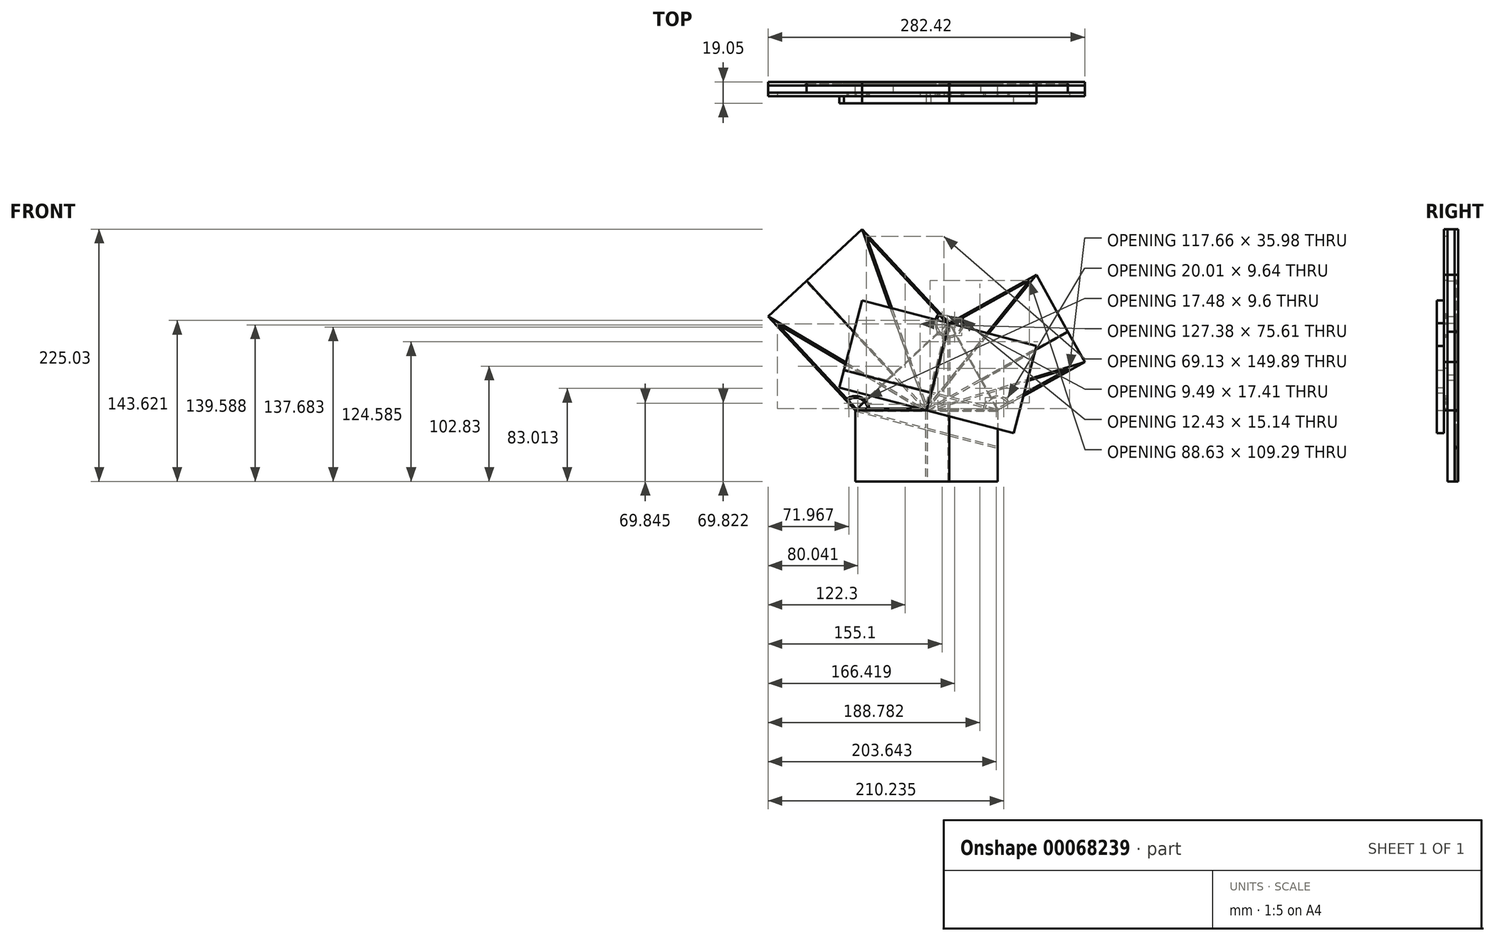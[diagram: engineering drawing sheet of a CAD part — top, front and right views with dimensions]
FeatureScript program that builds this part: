
annotation { "Feature Type Name" : "Feature", "Feature Type Description" : "" }
export const myFeature = defineFeature(function(context is Context, id is Id, definition is map)
    precondition{}
    {
        {
            var Q0;
            Q0=qCreatedBy(makeId("Front.planeOp"),FACE);
            var sketch = newSketch(context, id + "F0", { "sketchPlane" : qUnion([Q0])});
            skLineSegment(sketch, "E0", {"start": v(0, 0) * mm, "end": v(20.32, 77.7) * mm});
            skLineSegment(sketch, "E1", {"start": v(-63.5, 0) * mm, "end": v(63.5, 0) * mm, "construction": true});
            skLineSegment(sketch, "E2", {"start": v(63.5, 0) * mm, "end": v(20.32, 77.7) * mm});
            skLineSegment(sketch, "E3", {"start": v(20.32, 77.7) * mm, "end": v(-63.5, 0) * mm});
            skLineSegment(sketch, "E4.top", {"start": v(-63.5, -63.5) * mm, "end": v(63.5, -63.5) * mm});
            skLineSegment(sketch, "E4.left", {"start": v(-63.5, 0) * mm, "end": v(-63.5, -63.5) * mm});
            skLineSegment(sketch, "E4.right", {"start": v(63.5, 0) * mm, "end": v(63.5, -63.5) * mm});
            skLineSegment(sketch, "E5", {"start": v(-63.5, 0) * mm, "end": v(-141.2, 83.82) * mm});
            skLineSegment(sketch, "E6", {"start": v(-141.2, 83.82) * mm, "end": v(-57.39, 161.53) * mm});
            skLineSegment(sketch, "E7", {"start": v(-57.39, 161.53) * mm, "end": v(20.32, 77.7) * mm});
            skLineSegment(sketch, "E8", {"start": v(20.32, 77.7) * mm, "end": v(98.03, 120.89) * mm});
            skLineSegment(sketch, "E9", {"start": v(98.03, 120.89) * mm, "end": v(141.2, 43.18) * mm});
            skLineSegment(sketch, "E10", {"start": v(141.2, 43.18) * mm, "end": v(63.5, 0) * mm});
            skLineSegment(sketch, "E11", {"start": v(20.32, 77.7) * mm, "end": v(20.32, -63.5) * mm, "construction": true});
            skLineSegment(sketch, "E12", {"start": v(0, 0) * mm, "end": v(126.23, 70.14) * mm, "construction": true});
            skLineSegment(sketch, "E13", {"start": v(0, 0) * mm, "end": v(-107.06, 115.48) * mm, "construction": true});
            skLineSegment(sketch, "E14", {"start": v(0, 0) * mm, "end": v(-63.5, 0) * mm});
            skLineSegment(sketch, "E15", {"start": v(0, 0) * mm, "end": v(63.5, 0) * mm});
            skLineSegment(sketch, "E16", {"start": v(20.32, 77.7) * mm, "end": v(98.03, 57.39) * mm, "construction": true});
            skLineSegment(sketch, "E17", {"start": v(98.03, 57.39) * mm, "end": v(77.7, -20.32) * mm, "construction": true});
            skLineSegment(sketch, "E18", {"start": v(77.7, -20.32) * mm, "end": v(0, 0) * mm, "construction": true});
            skLineSegment(sketch, "E19", {"start": v(20.32, 77.7) * mm, "end": v(-57.39, 98.03) * mm, "construction": true});
            skLineSegment(sketch, "E20", {"start": v(-57.39, 98.03) * mm, "end": v(-77.7, 20.32) * mm, "construction": true});
            skLineSegment(sketch, "E21", {"start": v(-77.7, 20.32) * mm, "end": v(0, 0) * mm, "construction": true});
            skLineSegment(sketch, "E22", {"start": v(63.5, 0) * mm, "end": v(4.06, 15.54) * mm, "construction": true});
            skLineSegment(sketch, "E23", {"start": v(4.06, 15.54) * mm, "end": v(-73.65, 35.86) * mm, "construction": true});
            skLineSegment(sketch, "E24", {"start": v(0, 0) * mm, "end": v(0, -63.5) * mm, "construction": true});
            skLineSegment(sketch, "E25", {"start": v(77.7, -20.32) * mm, "end": v(73.65, -35.86) * mm, "construction": true});
            skLineSegment(sketch, "E26", {"start": v(73.65, -35.86) * mm, "end": v(-63.5, 0) * mm, "construction": true});
            skLineSegment(sketch, "E27", {"start": v(0, 0) * mm, "end": v(-4.06, -15.54) * mm, "construction": true});
            skLineSegment(sketch, "E28", {"start": v(20.32, 0) * mm, "end": v(20.32, -63.5) * mm});
            skLineSegment(sketch, "E29", {"start": v(126.23, 70.14) * mm, "end": v(48.52, 26.96) * mm});
            skLineSegment(sketch, "E30", {"start": v(-107.06, 115.48) * mm, "end": v(-29.35, 31.66) * mm});
            skSolve(sketch);
        }
        {
            var Q0;
            {var subQ0=sQuery(id+"F0.wireOp",EDGE,"E0");Q0=makeQuery(id+"F0.imprint","IMPRINT",FACE,{"disambiguationData":[TD([[makeQuery(id+"F0.imprint","IMPRINT",EDGE,{"derivedFrom":subQ0}),1.0]])]});}
            var Q1;
            {var subQ1=sQuery(id+"F0.wireOp",EDGE,"E0");Q1=makeQuery(id+"F0.imprint","IMPRINT",FACE,{"disambiguationData":[TD([[makeQuery(id+"F0.imprint","IMPRINT",EDGE,{"derivedFrom":subQ1}),-1.0]])]});}
            var Q2;
            {var subQ0=sQuery(id+"F0.wireOp",EDGE,"E7");Q2=makeQuery(id+"F0.imprint","IMPRINT",FACE,{"disambiguationData":[TD([[makeQuery(id+"F0.imprint","IMPRINT",EDGE,{"derivedFrom":subQ0}),-1.0]])]});}
            var Q3;
            {var subQ0=sQuery(id+"F0.wireOp",EDGE,"E5");Q3=makeQuery(id+"F0.imprint","IMPRINT",FACE,{"disambiguationData":[TD([[makeQuery(id+"F0.imprint","IMPRINT",EDGE,{"derivedFrom":subQ0}),-1.0]])]});}
            var Q4;
            {var subQ0=sQuery(id+"F0.wireOp",EDGE,"E8");Q4=makeQuery(id+"F0.imprint","IMPRINT",FACE,{"disambiguationData":[TD([[makeQuery(id+"F0.imprint","IMPRINT",EDGE,{"derivedFrom":subQ0}),-1.0]])]});}
            var Q5;
            {var subQ0=sQuery(id+"F0.wireOp",EDGE,"E10");Q5=makeQuery(id+"F0.imprint","IMPRINT",FACE,{"disambiguationData":[TD([[makeQuery(id+"F0.imprint","IMPRINT",EDGE,{"derivedFrom":subQ0}),-1.0]])]});}
            var Q6;
            {var subQ0=sQuery(id+"F0.wireOp",EDGE,"E4.right");Q6=makeQuery(id+"F0.imprint","IMPRINT",FACE,{"disambiguationData":[TD([[makeQuery(id+"F0.imprint","IMPRINT",EDGE,{"derivedFrom":subQ0}),-1.0]])]});}
            var Q7;
            {var subQ3=sQuery(id+"F0.wireOp",EDGE,"E4.left");Q7=makeQuery(id+"F0.imprint","IMPRINT",FACE,{"disambiguationData":[TD([[makeQuery(id+"F0.imprint","IMPRINT",EDGE,{"derivedFrom":subQ3}),1.0]])]});}
            extrude(context, id + "F1", {"entities" : qUnion([Q0, Q1, Q2, Q3, Q4, Q5, Q6, Q7]), "oppositeDirection" : true, "depth" : 3.17 * mm});
        }
        {
            var Q0;
            Q0=makeQuery(id+"F1.opExtrude","CAP_FACE",FACE,{"disambiguationData":[OSD([sQuery(id+"F0.wireOp",EDGE,"E4.top"),sQuery(id+"F0.wireOp",EDGE,"E4.left"),sQuery(id+"F0.wireOp",EDGE,"E4.right"),sQuery(id+"F0.wireOp",EDGE,"E5"),sQuery(id+"F0.wireOp",EDGE,"E6"),sQuery(id+"F0.wireOp",EDGE,"E7"),sQuery(id+"F0.wireOp",EDGE,"E8"),sQuery(id+"F0.wireOp",EDGE,"E9"),sQuery(id+"F0.wireOp",EDGE,"E10")])],"isStart":true});
            var sketch = newSketch(context, id + "F2", { "sketchPlane" : qUnion([Q0])});
            skLineSegment(sketch, "E31", {"start": v(20.32, 77.7) * mm, "end": v(-63.5, 0) * mm});
            skLineSegment(sketch, "E32", {"start": v(-63.5, 0) * mm, "end": v(63.5, 0) * mm});
            skLineSegment(sketch, "E33", {"start": v(63.5, 0) * mm, "end": v(20.32, 77.7) * mm});
            skArc(sketch, "E34.0.startCap", {"start": v(-63.5, -0.76) * mm, "mid": v(-64.26, 0) * mm, "end": v(-63.5, 0.76) * mm});
            skArc(sketch, "E34.0.endCap", {"start": v(63.5, 0.76) * mm, "mid": v(64.26, 0) * mm, "end": v(63.5, -0.76) * mm});
            skLineSegment(sketch, "E34.0.left", {"start": v(-63.5, 0.76) * mm, "end": v(62.2, 0.76) * mm});
            skLineSegment(sketch, "E34.0.right", {"start": v(-63.5, -0.76) * mm, "end": v(63.5, -0.76) * mm});
            skArc(sketch, "E34.1.startCap", {"start": v(19.8, 78.27) * mm, "mid": v(20.88, 78.23) * mm, "end": v(20.84, 77.15) * mm});
            skArc(sketch, "E34.1.endCap", {"start": v(-62.98, -0.56) * mm, "mid": v(-64.06, -0.52) * mm, "end": v(-64.02, 0.56) * mm});
            skLineSegment(sketch, "E34.1.left", {"start": v(20.84, 77.15) * mm, "end": v(20.7, 77.02) * mm});
            skLineSegment(sketch, "E34.1.right", {"start": v(19.8, 78.27) * mm, "end": v(-64.02, 0.56) * mm});
            skArc(sketch, "E34.2.startCap", {"start": v(64.17, 0.37) * mm, "mid": v(63.87, -0.67) * mm, "end": v(62.83, -0.37) * mm});
            skArc(sketch, "E34.2.endCap", {"start": v(19.65, 77.34) * mm, "mid": v(19.95, 78.38) * mm, "end": v(20.99, 78.08) * mm});
            skLineSegment(sketch, "E34.2.left", {"start": v(62.83, -0.37) * mm, "end": v(19.65, 77.34) * mm});
            skLineSegment(sketch, "E34.2.right", {"start": v(64.17, 0.37) * mm, "end": v(20.99, 78.08) * mm});
            skLineSegment(sketch, "E35.trimOffspring", {"start": v(20.13, 76.49) * mm, "end": v(-62.98, -0.56) * mm});
            skLineSegment(sketch, "E36.trimOffspring", {"start": v(63.08, 0.76) * mm, "end": v(63.5, 0.76) * mm});
            skSolve(sketch);
        }
        {
            var Q0;
            Q0=makeQuery(id+"F1.opExtrude","CAP_FACE",FACE,{"disambiguationData":[OSD([sQuery(id+"F0.wireOp",EDGE,"E4.top"),sQuery(id+"F0.wireOp",EDGE,"E4.left"),sQuery(id+"F0.wireOp",EDGE,"E4.right"),sQuery(id+"F0.wireOp",EDGE,"E5"),sQuery(id+"F0.wireOp",EDGE,"E6"),sQuery(id+"F0.wireOp",EDGE,"E7"),sQuery(id+"F0.wireOp",EDGE,"E8"),sQuery(id+"F0.wireOp",EDGE,"E9"),sQuery(id+"F0.wireOp",EDGE,"E10")])],"isStart":true});
            var sketch = newSketch(context, id + "F3", { "sketchPlane" : qUnion([Q0])});
            skLineSegment(sketch, "E37", {"start": v(20.32, 77.7) * mm, "end": v(0, 0) * mm});
            skLineSegment(sketch, "E38", {"start": v(0, 0) * mm, "end": v(0, -63.5) * mm});
            skArc(sketch, "E39.0.startCap", {"start": v(19.58, 77.9) * mm, "mid": v(20.51, 78.45) * mm, "end": v(21.06, 77.52) * mm});
            skArc(sketch, "E39.0.endCap", {"start": v(0.74, -0.2) * mm, "mid": v(-0.2, -0.74) * mm, "end": v(-0.74, 0.2) * mm});
            skLineSegment(sketch, "E39.0.left", {"start": v(21.06, 77.52) * mm, "end": v(0.74, -0.2) * mm});
            skLineSegment(sketch, "E39.0.right", {"start": v(19.58, 77.9) * mm, "end": v(-0.74, 0.2) * mm});
            skArc(sketch, "E39.1.startCap", {"start": v(-0.76, 0) * mm, "mid": v(0, 0.76) * mm, "end": v(0.76, 0) * mm});
            skArc(sketch, "E39.1.endCap", {"start": v(0.76, -63.5) * mm, "mid": v(0, -64.26) * mm, "end": v(-0.76, -63.5) * mm});
            skLineSegment(sketch, "E39.1.left", {"start": v(0.76, 0) * mm, "end": v(0.76, -63.5) * mm});
            skLineSegment(sketch, "E39.1.right", {"start": v(-0.76, 0) * mm, "end": v(-0.76, -63.5) * mm});
            skLineSegment(sketch, "E40", {"start": v(63.5, 0) * mm, "end": v(-73.65, 35.86) * mm});
            skArc(sketch, "E41.0.startCap", {"start": v(63.7, 0.74) * mm, "mid": v(64.24, -0.2) * mm, "end": v(63.3, -0.74) * mm});
            skArc(sketch, "E41.0.endCap", {"start": v(-73.84, 35.12) * mm, "mid": v(-74.38, 36.05) * mm, "end": v(-73.45, 36.6) * mm});
            skLineSegment(sketch, "E41.0.left", {"start": v(63.3, -0.74) * mm, "end": v(-73.84, 35.12) * mm});
            skLineSegment(sketch, "E41.0.right", {"start": v(63.7, 0.74) * mm, "end": v(-73.45, 36.6) * mm});
            skLineSegment(sketch, "E42", {"start": v(-63.5, 0) * mm, "end": v(73.65, -35.86) * mm});
            skArc(sketch, "E43.0.startCap", {"start": v(-63.7, -0.74) * mm, "mid": v(-64.24, 0.2) * mm, "end": v(-63.3, 0.74) * mm});
            skArc(sketch, "E43.0.endCap", {"start": v(73.84, -35.12) * mm, "mid": v(74.38, -36.05) * mm, "end": v(73.45, -36.6) * mm});
            skLineSegment(sketch, "E43.0.left", {"start": v(-63.3, 0.74) * mm, "end": v(73.84, -35.12) * mm});
            skLineSegment(sketch, "E43.0.right", {"start": v(-63.7, -0.74) * mm, "end": v(73.45, -36.6) * mm});
            skSolve(sketch);
        }
        {
            var Q0;
            {var subQ2=sQuery(id+"F3.wireOp",EDGE,"E39.0.right");Q0=makeQuery(id+"F3.imprint","IMPRINT",FACE,{"disambiguationData":[TD([[makeQuery(id+"F3.imprint","IMPRINT",EDGE,{"derivedFrom":subQ2}),-1.0]])]});}
            var sketch = newSketch(context, id + "F4", { "sketchPlane" : qUnion([Q0])});
            skLineSegment(sketch, "E44", {"start": v(0, 0) * mm, "end": v(126.23, 70.14) * mm});
            skLineSegment(sketch, "E45", {"start": v(0, 0) * mm, "end": v(-107.06, 115.48) * mm});
            skLineSegment(sketch, "E46", {"start": v(20.32, -63.5) * mm, "end": v(20.32, 77.7) * mm});
            skArc(sketch, "E47.0.startCap", {"start": v(21.08, -63.5) * mm, "mid": v(20.32, -64.26) * mm, "end": v(19.56, -63.5) * mm});
            skArc(sketch, "E47.0.endCap", {"start": v(19.56, 77.7) * mm, "mid": v(20.32, 78.47) * mm, "end": v(21.08, 77.7) * mm});
            skLineSegment(sketch, "E47.0.left", {"start": v(19.56, -63.5) * mm, "end": v(19.56, 77.7) * mm});
            skLineSegment(sketch, "E47.0.right", {"start": v(21.08, -63.5) * mm, "end": v(21.08, 77.7) * mm});
            skArc(sketch, "E47.1.startCap", {"start": v(0.56, 0.52) * mm, "mid": v(0.52, -0.56) * mm, "end": v(-0.56, -0.52) * mm});
            skArc(sketch, "E47.1.endCap", {"start": v(-107.62, 114.96) * mm, "mid": v(-107.58, 116.04) * mm, "end": v(-106.5, 116) * mm});
            skLineSegment(sketch, "E47.1.left", {"start": v(-0.56, -0.52) * mm, "end": v(-107.62, 114.96) * mm});
            skLineSegment(sketch, "E47.1.right", {"start": v(0.56, 0.52) * mm, "end": v(-106.5, 116) * mm});
            skArc(sketch, "E47.2.startCap", {"start": v(0.37, -0.67) * mm, "mid": v(-0.67, -0.37) * mm, "end": v(-0.37, 0.67) * mm});
            skArc(sketch, "E47.2.endCap", {"start": v(125.86, 70.8) * mm, "mid": v(126.9, 70.51) * mm, "end": v(126.6, 69.47) * mm});
            skLineSegment(sketch, "E47.2.left", {"start": v(-0.37, 0.67) * mm, "end": v(125.86, 70.8) * mm});
            skLineSegment(sketch, "E47.2.right", {"start": v(0.37, -0.67) * mm, "end": v(126.6, 69.47) * mm});
            skSolve(sketch);
        }
        {
            var Q0;
            Q0 = qSketchRegion(id + "F2", true);
            var Q1;
            Q1 = qSketchRegion(id + "F3", true);
            var Q2;
            Q2 = qSketchRegion(id + "F4", true);
            extrude(context, id + "F5", {"entities" : qUnion([Q0, Q1, Q2]), "operationType" : NewBodyOperationType.REMOVE, "oppositeDirection" : true, "depth" : 1.52 * mm});
        }
        {
            var Q0;
            {var subQ0=sQuery(id+"F0.wireOp",EDGE,"E0");Q0=makeQuery(id+"F0.imprint","IMPRINT",FACE,{"disambiguationData":[TD([[makeQuery(id+"F0.imprint","IMPRINT",EDGE,{"derivedFrom":subQ0}),1.0]])]});}
            var Q1;
            {var subQ1=sQuery(id+"F0.wireOp",EDGE,"E0");Q1=makeQuery(id+"F0.imprint","IMPRINT",FACE,{"disambiguationData":[TD([[makeQuery(id+"F0.imprint","IMPRINT",EDGE,{"derivedFrom":subQ1}),-1.0]])]});}
            extrude(context, id + "F6", {"entities" : qUnion([Q0, Q1]), "depth" : 9.52 * mm});
        }
        {
            var Q0;
            {var subQ0=sQuery(id+"F0.wireOp",EDGE,"E5");Q0=makeQuery(id+"F0.imprint","IMPRINT",FACE,{"disambiguationData":[TD([[makeQuery(id+"F0.imprint","IMPRINT",EDGE,{"derivedFrom":subQ0}),-1.0]])]});}
            var Q1;
            {var subQ3=sQuery(id+"F0.wireOp",EDGE,"E4.left");Q1=makeQuery(id+"F0.imprint","IMPRINT",FACE,{"disambiguationData":[TD([[makeQuery(id+"F0.imprint","IMPRINT",EDGE,{"derivedFrom":subQ3}),1.0]])]});}
            extrude(context, id + "F7", {"entities" : qUnion([Q0, Q1]), "depth" : 6.35 * mm});
        }
        {
            var Q0;
            {var subQ0=sQuery(id+"F0.wireOp",EDGE,"E10");Q0=makeQuery(id+"F0.imprint","IMPRINT",FACE,{"disambiguationData":[TD([[makeQuery(id+"F0.imprint","IMPRINT",EDGE,{"derivedFrom":subQ0}),-1.0]])]});}
            var Q1;
            {var subQ0=sQuery(id+"F0.wireOp",EDGE,"E4.right");Q1=makeQuery(id+"F0.imprint","IMPRINT",FACE,{"disambiguationData":[TD([[makeQuery(id+"F0.imprint","IMPRINT",EDGE,{"derivedFrom":subQ0}),-1.0]])]});}
            extrude(context, id + "F8", {"entities" : qUnion([Q0, Q1]), "depth" : 6.35 * mm});
        }
        {
            var Q0;
            {var subQ0=sQuery(id+"F0.wireOp",EDGE,"E7");Q0=makeQuery(id+"F0.imprint","IMPRINT",FACE,{"disambiguationData":[TD([[makeQuery(id+"F0.imprint","IMPRINT",EDGE,{"derivedFrom":subQ0}),-1.0]])]});}
            var Q1;
            {var subQ0=sQuery(id+"F0.wireOp",EDGE,"E8");Q1=makeQuery(id+"F0.imprint","IMPRINT",FACE,{"disambiguationData":[TD([[makeQuery(id+"F0.imprint","IMPRINT",EDGE,{"derivedFrom":subQ0}),-1.0]])]});}
            extrude(context, id + "F9", {"entities" : qUnion([Q0, Q1]), "depth" : 6.35 * mm});
        }
        {
            var Q0;
            Q0=makeQuery(id+"F6.opExtrude","CAP_FACE",FACE,{"disambiguationData":[OSD([sQuery(id+"F0.wireOp",EDGE,"E2"),sQuery(id+"F0.wireOp",EDGE,"E3"),sQuery(id+"F0.wireOp",EDGE,"E14"),sQuery(id+"F0.wireOp",EDGE,"E15")])],"isStart":false});
            var sketch = newSketch(context, id + "F10", { "sketchPlane" : qUnion([Q0])});
            skLineSegment(sketch, "E48", {"start": v(20.32, 77.7) * mm, "end": v(-57.39, 98.03) * mm});
            skLineSegment(sketch, "E49", {"start": v(-57.39, 98.03) * mm, "end": v(-73.65, 35.86) * mm});
            skLineSegment(sketch, "E50", {"start": v(-73.65, 35.86) * mm, "end": v(4.06, 15.54) * mm});
            skLineSegment(sketch, "E51", {"start": v(4.06, 15.54) * mm, "end": v(20.32, 77.7) * mm});
            skLineSegment(sketch, "E52", {"start": v(4.06, 15.54) * mm, "end": v(0, 0) * mm});
            skLineSegment(sketch, "E53", {"start": v(0, 0) * mm, "end": v(77.7, -20.32) * mm});
            skLineSegment(sketch, "E54", {"start": v(20.32, 77.7) * mm, "end": v(98.03, 57.39) * mm});
            skLineSegment(sketch, "E55", {"start": v(77.7, -20.32) * mm, "end": v(98.03, 57.39) * mm});
            skLineSegment(sketch, "E56", {"start": v(0, 0) * mm, "end": v(-77.7, 20.32) * mm});
            skLineSegment(sketch, "E57", {"start": v(-77.7, 20.32) * mm, "end": v(-73.65, 35.86) * mm});
            skLineSegment(sketch, "E58.0", {"start": v(77.7, -20.32) * mm, "end": v(73.65, -35.86) * mm});
            skLineSegment(sketch, "E58.1", {"start": v(73.65, -35.86) * mm, "end": v(-4.06, -15.54) * mm});
            skLineSegment(sketch, "E58.2", {"start": v(0, 0) * mm, "end": v(-4.06, -15.54) * mm});
            skPoint(sketch, "E59.orphan", {"position": v(-63.5, 0) * mm});
            skSolve(sketch);
        }
        {
            var Q0;
            Q0=sQuery(id+"F10.wireOp",EDGE,"E55");
            var Q1;
            Q1=sQuery(id+"F10.wireOp",EDGE,"E54");
            var Q2;
            Q2=sQuery(id+"F10.wireOp",EDGE,"E51");
            var Q3;
            Q3=sQuery(id+"F10.wireOp",EDGE,"E52");
            var Q4;
            Q4=sQuery(id+"F10.wireOp",EDGE,"E58.0");
            var Q5;
            Q5=sQuery(id+"F10.wireOp",EDGE,"E58.1");
            var Q6;
            Q6=sQuery(id+"F10.wireOp",EDGE,"E58.2");
            extrude(context, id + "F11", {"bodyType" : ExtendedToolBodyType.SURFACE, "surfaceEntities" : qUnion([Q0, Q1, Q2, Q3, Q4, Q5, Q6]), "depth" : 6.35 * mm});
        }
        {
            var Q0;
            Q0=makeQuery(id+"F10.imprint","IMPRINT",FACE,{"disambiguationData":[TD([[makeQuery(id+"F10.imprint","IMPRINT",EDGE,{"derivedFrom":sQuery(id+"F10.wireOp",EDGE,"E51")}),-1.0]])]});
            var sketch = newSketch(context, id + "F12", { "sketchPlane" : qUnion([Q0])});
            skLineSegment(sketch, "E60.0", {"start": v(20.32, 77.7) * mm, "end": v(98.03, 57.39) * mm});
            skLineSegment(sketch, "E60.1", {"start": v(77.7, -20.32) * mm, "end": v(98.03, 57.39) * mm});
            skLineSegment(sketch, "E60.2", {"start": v(0, 0) * mm, "end": v(77.7, -20.32) * mm});
            skLineSegment(sketch, "E60.3", {"start": v(4.06, 15.54) * mm, "end": v(20.32, 77.7) * mm});
            skLineSegment(sketch, "E60.4", {"start": v(4.06, 15.54) * mm, "end": v(0, 0) * mm});
            skSolve(sketch);
        }
        {
            var Q0;
            Q0 = qSketchRegion(id + "F12", true);
            extrude(context, id + "F13", {"entities" : qUnion([Q0]), "depth" : 6.35 * mm});
        }
        {
            var Q0;
            Q0=makeQuery(id+"F10.imprint","IMPRINT",FACE,{"disambiguationData":[TD([[makeQuery(id+"F10.imprint","IMPRINT",EDGE,{"derivedFrom":sQuery(id+"F10.wireOp",EDGE,"E51")}),-1.0]])]});
            var sketch = newSketch(context, id + "F14", { "sketchPlane" : qUnion([Q0])});
            skLineSegment(sketch, "E61.0", {"start": v(4.06, 15.54) * mm, "end": v(20.32, 77.7) * mm});
            skLineSegment(sketch, "E61.1", {"start": v(20.32, 77.7) * mm, "end": v(-57.39, 98.03) * mm});
            skLineSegment(sketch, "E61.2", {"start": v(-57.39, 98.03) * mm, "end": v(-73.65, 35.86) * mm});
            skLineSegment(sketch, "E61.3", {"start": v(-73.65, 35.86) * mm, "end": v(4.06, 15.54) * mm});
            skSolve(sketch);
        }
        {
            var Q0;
            Q0 = qSketchRegion(id + "F14", true);
            extrude(context, id + "F15", {"entities" : qUnion([Q0]), "depth" : 6.35 * mm});
        }
        {
            var Q0;
            Q0=makeQuery(id+"F10.imprint","IMPRINT",FACE,{"disambiguationData":[TD([[makeQuery(id+"F10.imprint","IMPRINT",EDGE,{"derivedFrom":sQuery(id+"F10.wireOp",EDGE,"E51")}),-1.0]])]});
            var sketch = newSketch(context, id + "F16", { "sketchPlane" : qUnion([Q0])});
            skLineSegment(sketch, "E62.0", {"start": v(4.06, 15.54) * mm, "end": v(0, 0) * mm});
            skLineSegment(sketch, "E62.1", {"start": v(-73.65, 35.86) * mm, "end": v(4.06, 15.54) * mm});
            skLineSegment(sketch, "E62.2", {"start": v(-77.7, 20.32) * mm, "end": v(-73.65, 35.86) * mm});
            skLineSegment(sketch, "E62.3", {"start": v(0, 0) * mm, "end": v(-77.7, 20.32) * mm});
            skSolve(sketch);
        }
        {
            var Q0;
            Q0 = qSketchRegion(id + "F16", true);
            extrude(context, id + "F17", {"entities" : qUnion([Q0]), "depth" : 6.35 * mm});
        }
        {
            var Q0;
            Q0=makeQuery(id+"F10.imprint","IMPRINT",FACE,{"disambiguationData":[TD([[makeQuery(id+"F10.imprint","IMPRINT",EDGE,{"derivedFrom":sQuery(id+"F10.wireOp",EDGE,"E51")}),-1.0]])]});
            var sketch = newSketch(context, id + "F18", { "sketchPlane" : qUnion([Q0])});
            skLineSegment(sketch, "E63.0", {"start": v(0, 0) * mm, "end": v(-63.5, 0) * mm});
            skLineSegment(sketch, "E63.1", {"start": v(-63.5, 0) * mm, "end": v(-141.2, 83.82) * mm});
            skLineSegment(sketch, "E64", {"start": v(-141.2, 83.82) * mm, "end": v(0, 0) * mm});
            skLineSegment(sketch, "E65.0", {"start": v(-132.93, 77.14) * mm, "end": v(-5.55, 1.52) * mm});
            skLineSegment(sketch, "E65.1", {"start": v(-62.83, 1.52) * mm, "end": v(-69.9, 9.16) * mm});
            skLineSegment(sketch, "E65.2", {"start": v(-5.55, 1.52) * mm, "end": v(-50.9, 1.52) * mm});
            skArc(sketch, "E66", {"start": v(-50.9, 1.52) * mm, "mid": v(-58.42, 11.64) * mm, "end": v(-70.95, 10.28) * mm});
            skArc(sketch, "E67.0", {"start": v(-52.43, 1.52) * mm, "mid": v(-59.03, 10.24) * mm, "end": v(-69.9, 9.16) * mm});
            skLineSegment(sketch, "E68.trimOffspring", {"start": v(-70.95, 10.28) * mm, "end": v(-132.93, 77.14) * mm});
            skLineSegment(sketch, "E69.trimOffspring", {"start": v(-52.43, 1.52) * mm, "end": v(-62.83, 1.52) * mm});
            skSolve(sketch);
        }
        {
            var Q0;
            Q0 = qSketchRegion(id + "F18", true);
            extrude(context, id + "F19", {"entities" : qUnion([Q0]), "oppositeDirection" : true, "depth" : 3.17 * mm});
        }
        {
            var Q0;
            Q0=makeQuery(id+"F6.opExtrude","CAP_FACE",FACE,{"disambiguationData":[OSD([sQuery(id+"F0.wireOp",EDGE,"E2"),sQuery(id+"F0.wireOp",EDGE,"E3"),sQuery(id+"F0.wireOp",EDGE,"E14"),sQuery(id+"F0.wireOp",EDGE,"E15")])],"isStart":false});
            var sketch = newSketch(context, id + "F20", { "sketchPlane" : qUnion([Q0])});
            skLineSegment(sketch, "E70.0", {"start": v(0, 0) * mm, "end": v(63.5, 0) * mm});
            skLineSegment(sketch, "E70.1", {"start": v(141.2, 43.18) * mm, "end": v(63.5, 0) * mm});
            skLineSegment(sketch, "E71", {"start": v(0, 0) * mm, "end": v(141.2, 43.18) * mm});
            skLineSegment(sketch, "E72.0", {"start": v(10.2, 1.52) * mm, "end": v(127.85, 37.5) * mm});
            skLineSegment(sketch, "E72.1", {"start": v(10.2, 1.52) * mm, "end": v(50.9, 1.52) * mm});
            skLineSegment(sketch, "E72.2", {"start": v(127.85, 37.5) * mm, "end": v(73.78, 7.46) * mm});
            skArc(sketch, "E73", {"start": v(73.78, 7.46) * mm, "mid": v(60.31, 12.3) * mm, "end": v(50.9, 1.52) * mm});
            skArc(sketch, "E74.0", {"start": v(72.44, 6.7) * mm, "mid": v(60.7, 10.82) * mm, "end": v(52.43, 1.52) * mm});
            skLineSegment(sketch, "E75.trimOffspring", {"start": v(72.44, 6.7) * mm, "end": v(63.1, 1.52) * mm});
            skLineSegment(sketch, "E76.trimOffspring", {"start": v(52.43, 1.52) * mm, "end": v(63.1, 1.52) * mm});
            skSolve(sketch);
        }
        {
            var Q0;
            Q0 = qSketchRegion(id + "F20", true);
            extrude(context, id + "F21", {"entities" : qUnion([Q0]), "oppositeDirection" : true, "depth" : 3.17 * mm});
        }
        {
            var Q0;
            Q0=makeQuery(id+"F6.opExtrude","CAP_FACE",FACE,{"disambiguationData":[OSD([sQuery(id+"F0.wireOp",EDGE,"E2"),sQuery(id+"F0.wireOp",EDGE,"E3"),sQuery(id+"F0.wireOp",EDGE,"E14"),sQuery(id+"F0.wireOp",EDGE,"E15")])],"isStart":false});
            var sketch = newSketch(context, id + "F22", { "sketchPlane" : qUnion([Q0])});
            skLineSegment(sketch, "E77.0", {"start": v(0, 0) * mm, "end": v(20.32, 77.7) * mm});
            skLineSegment(sketch, "E77.1", {"start": v(20.32, 77.7) * mm, "end": v(98.03, 120.89) * mm});
            skLineSegment(sketch, "E78", {"start": v(98.03, 120.89) * mm, "end": v(0, 0) * mm});
            skLineSegment(sketch, "E79.0", {"start": v(21.63, 76.7) * mm, "end": v(30.74, 81.75) * mm});
            skLineSegment(sketch, "E79.1", {"start": v(3.26, 6.44) * mm, "end": v(18.6, 65.13) * mm});
            skLineSegment(sketch, "E79.2", {"start": v(91.88, 115.73) * mm, "end": v(3.26, 6.44) * mm});
            skArc(sketch, "E80", {"start": v(32.08, 82.5) * mm, "mid": v(30.36, 69.93) * mm, "end": v(18.6, 65.13) * mm});
            skArc(sketch, "E81.0", {"start": v(30.74, 81.75) * mm, "mid": v(29.15, 70.86) * mm, "end": v(19, 66.61) * mm});
            skLineSegment(sketch, "E82.trimOffspring", {"start": v(32.08, 82.5) * mm, "end": v(91.88, 115.73) * mm});
            skLineSegment(sketch, "E83.trimOffspring", {"start": v(19, 66.61) * mm, "end": v(21.63, 76.7) * mm});
            skSolve(sketch);
        }
        {
            var Q0;
            Q0 = qSketchRegion(id + "F22", true);
            extrude(context, id + "F23", {"entities" : qUnion([Q0]), "oppositeDirection" : true, "depth" : 3.17 * mm});
        }
        {
            var Q0;
            Q0=makeQuery(id+"F6.opExtrude","CAP_FACE",FACE,{"disambiguationData":[OSD([sQuery(id+"F0.wireOp",EDGE,"E2"),sQuery(id+"F0.wireOp",EDGE,"E3"),sQuery(id+"F0.wireOp",EDGE,"E14"),sQuery(id+"F0.wireOp",EDGE,"E15")])],"isStart":false});
            var sketch = newSketch(context, id + "F24", { "sketchPlane" : qUnion([Q0])});
            skLineSegment(sketch, "E84.0", {"start": v(0, 0) * mm, "end": v(20.32, 77.7) * mm});
            skLineSegment(sketch, "E84.1", {"start": v(-57.39, 161.53) * mm, "end": v(20.32, 77.7) * mm});
            skLineSegment(sketch, "E85", {"start": v(-57.39, 161.53) * mm, "end": v(0, 0) * mm});
            skLineSegment(sketch, "E86.0", {"start": v(-53.48, 155.07) * mm, "end": v(10.63, 85.92) * mm});
            skLineSegment(sketch, "E86.1", {"start": v(-53.48, 155.07) * mm, "end": v(-0.22, 5.18) * mm});
            skLineSegment(sketch, "E86.2", {"start": v(-0.22, 5.18) * mm, "end": v(15.66, 65.9) * mm});
            skArc(sketch, "E87", {"start": v(10.63, 85.92) * mm, "mid": v(8, 74.62) * mm, "end": v(15.66, 65.9) * mm});
            skArc(sketch, "E88.0", {"start": v(11.68, 84.8) * mm, "mid": v(9.48, 74.99) * mm, "end": v(16.04, 67.38) * mm});
            skLineSegment(sketch, "E89.trimOffspring", {"start": v(11.68, 84.8) * mm, "end": v(18.63, 77.29) * mm});
            skLineSegment(sketch, "E90.trimOffspring", {"start": v(16.04, 67.38) * mm, "end": v(18.63, 77.29) * mm});
            skSolve(sketch);
        }
        {
            var Q0;
            Q0 = qSketchRegion(id + "F24", true);
            extrude(context, id + "F25", {"entities" : qUnion([Q0]), "oppositeDirection" : true, "depth" : 3.17 * mm});
        }
    });
